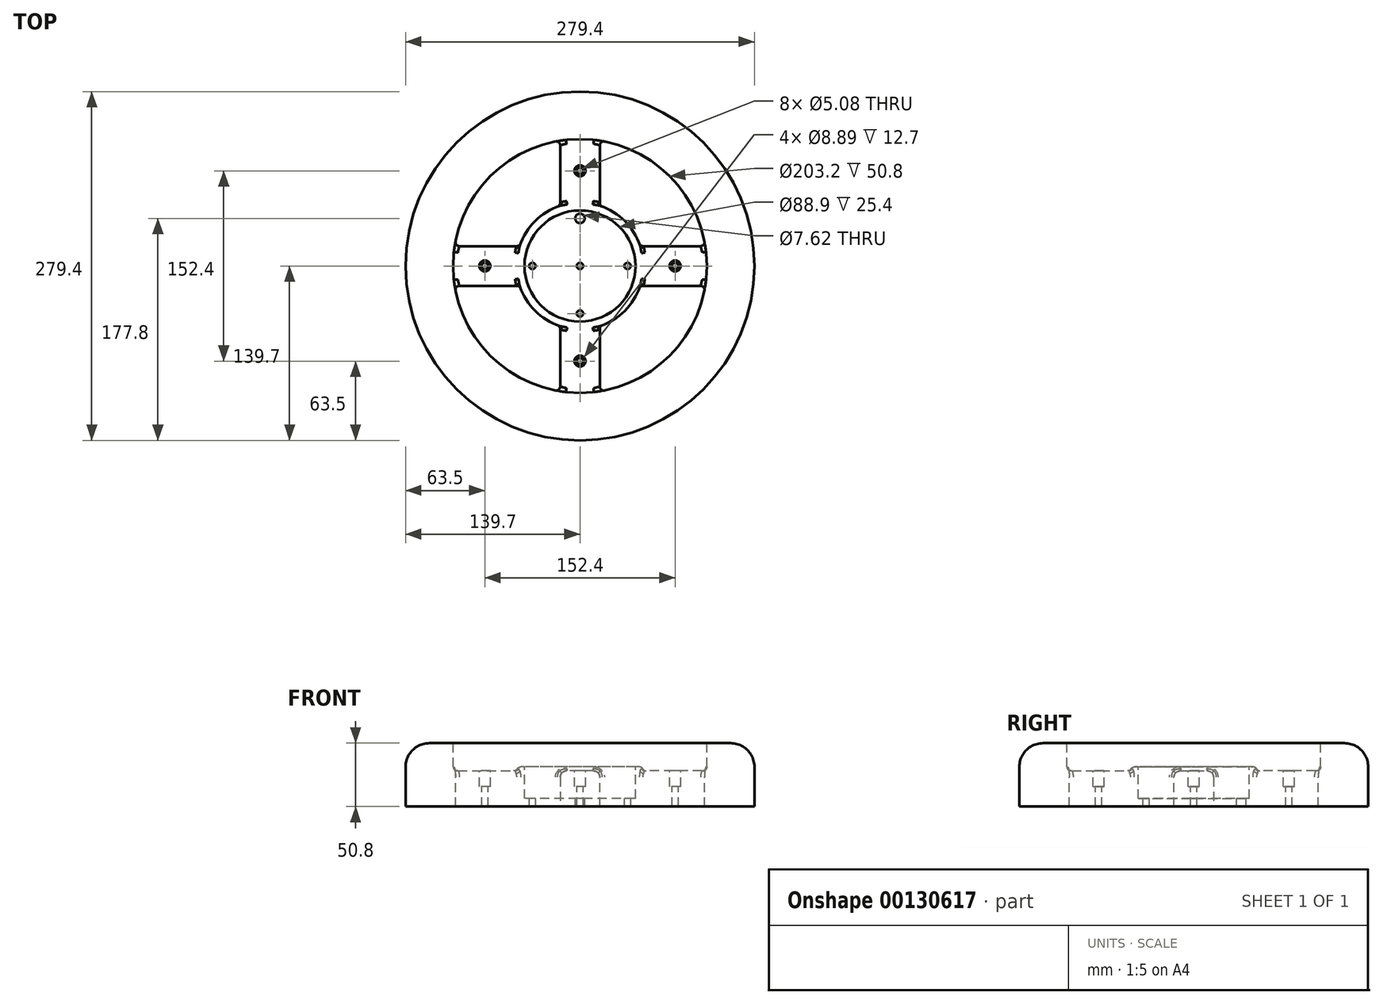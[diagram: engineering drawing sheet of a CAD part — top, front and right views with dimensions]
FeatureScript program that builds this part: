
annotation { "Feature Type Name" : "Feature", "Feature Type Description" : "" }
export const myFeature = defineFeature(function(context is Context, id is Id, definition is map)
    precondition{}
    {
        {
            var Q0;
            Q0=qCreatedBy(makeId("Top.planeOp"),FACE);
            var sketch = newSketch(context, id + "F0", { "sketchPlane" : qUnion([Q0])});
            skCircle(sketch, "E0", {"center": v(0, 0) * mm, "radius": 139.7 * mm});
            skSolve(sketch);
        }
        {
            var Q0;
            Q0 = qSketchRegion(id + "F0", true);
            extrude(context, id + "F1", {"entities" : qUnion([Q0]), "depth" : 50.8 * mm});
        }
        {
            var Q0;
            Q0=makeQuery(id+"F1.opExtrude","CAP_FACE",FACE,{"disambiguationData":[OSD([sQuery(id+"F0.wireOp",EDGE,"E0")])],"isStart":false});
            var sketch = newSketch(context, id + "F2", { "sketchPlane" : qUnion([Q0])});
            skCircle(sketch, "E1", {"center": v(0, 0) * mm, "radius": 101.6 * mm});
            skSolve(sketch);
        }
        {
            var Q0;
            Q0 = qSketchRegion(id + "F2", true);
            extrude(context, id + "F3", {"entities" : qUnion([Q0]), "operationType" : NewBodyOperationType.REMOVE, "oppositeDirection" : true, "depth" : 50.8 * mm});
        }
        {
            var Q0;
            Q0=makeQuery(id+"F1.opExtrude","CAP_EDGE",EDGE,{"disambiguationData":[OSD([sQuery(id+"F0.wireOp",EDGE,"E0")])],"isStart":false});
            var Q1;
            Q1=makeQuery(id+"F3.boolean.opBoolean","COPY",EDGE,{"derivedFrom":makeQuery(id+"F3.opExtrude","CAP_EDGE",EDGE,{"disambiguationData":[OSD([sQuery(id+"F2.wireOp",EDGE,"E1")])],"isStart":true})});
            fillet(context, id + "F4", {"entities" : qUnion([Q0, Q1]), "radius" : 19.05 * mm, "tangentPropagation" : true, "allowEdgeOverflow" : false});
        }
        {
            var Q0;
            Q0=qCreatedBy(makeId("Top.planeOp"),FACE);
            var sketch = newSketch(context, id + "F5", { "sketchPlane" : qUnion([Q0])});
            skCircle(sketch, "E2", {"center": v(0, 0) * mm, "radius": 50.8 * mm});
            skSolve(sketch);
        }
        {
            var Q0;
            Q0 = qSketchRegion(id + "F5", true);
            extrude(context, id + "F6", {"entities" : qUnion([Q0]), "depth" : 31.75 * mm});
        }
        {
            var Q0;
            Q0=makeQuery(id+"F6.opExtrude","CAP_FACE",FACE,{"disambiguationData":[OSD([sQuery(id+"F5.wireOp",EDGE,"E2")])],"isStart":false});
            var sketch = newSketch(context, id + "F7", { "sketchPlane" : qUnion([Q0])});
            skCircle(sketch, "E3", {"center": v(0, 0) * mm, "radius": 44.45 * mm});
            skSolve(sketch);
        }
        {
            var Q0;
            Q0 = qSketchRegion(id + "F7", true);
            extrude(context, id + "F8", {"entities" : qUnion([Q0]), "operationType" : NewBodyOperationType.REMOVE, "oppositeDirection" : true, "depth" : 25.4 * mm});
        }
        {
            var Q0;
            Q0=makeQuery(id+"F8.boolean.opBoolean","COPY",EDGE,{"derivedFrom":makeQuery(id+"F8.opExtrude","CAP_EDGE",EDGE,{"disambiguationData":[OSD([sQuery(id+"F7.wireOp",EDGE,"E3")])],"isStart":true})});
            var Q1;
            Q1=makeQuery(id+"F6.opExtrude","CAP_EDGE",EDGE,{"disambiguationData":[OSD([sQuery(id+"F5.wireOp",EDGE,"E2")])],"isStart":false});
            fillet(context, id + "F9", {"entities" : qUnion([Q0, Q1]), "radius" : 3.17 * mm, "tangentPropagation" : true, "allowEdgeOverflow" : false});
        }
        {
            var Q0;
            Q0=qCreatedBy(makeId("Top.planeOp"),FACE);
            var sketch = newSketch(context, id + "F10", { "sketchPlane" : qUnion([Q0])});
            skLineSegment(sketch, "E4.bottom", {"start": v(-15.87, 104.14) * mm, "end": v(15.88, 104.14) * mm});
            skLineSegment(sketch, "E4.top", {"start": v(-15.87, 47) * mm, "end": v(15.88, 47) * mm});
            skLineSegment(sketch, "E4.left", {"start": v(-15.87, 104.14) * mm, "end": v(-15.87, 47) * mm});
            skLineSegment(sketch, "E4.right", {"start": v(15.88, 104.14) * mm, "end": v(15.88, 47) * mm});
            skPoint(sketch, "E4.middle", {"position": v(0, 75.56) * mm});
            skLineSegment(sketch, "E5.bottom", {"start": v(15.88, -104.14) * mm, "end": v(-15.88, -104.14) * mm});
            skLineSegment(sketch, "E5.top", {"start": v(15.87, -47) * mm, "end": v(-15.88, -47) * mm});
            skLineSegment(sketch, "E5.left", {"start": v(15.88, -104.14) * mm, "end": v(15.87, -47) * mm});
            skLineSegment(sketch, "E5.right", {"start": v(-15.88, -104.14) * mm, "end": v(-15.88, -47) * mm});
            skPoint(sketch, "E5.middle", {"position": v(0, -75.56) * mm});
            skLineSegment(sketch, "E6.bottom", {"start": v(104.14, -15.87) * mm, "end": v(47, -15.87) * mm});
            skLineSegment(sketch, "E6.top", {"start": v(104.14, 15.88) * mm, "end": v(47, 15.88) * mm});
            skLineSegment(sketch, "E6.left", {"start": v(104.14, -15.87) * mm, "end": v(104.14, 15.88) * mm});
            skLineSegment(sketch, "E6.right", {"start": v(47, -15.87) * mm, "end": v(47, 15.88) * mm});
            skPoint(sketch, "E6.middle", {"position": v(75.56, 0) * mm});
            skLineSegment(sketch, "E7.bottom", {"start": v(-104.14, -15.88) * mm, "end": v(-47, -15.88) * mm});
            skLineSegment(sketch, "E7.top", {"start": v(-104.14, 15.88) * mm, "end": v(-47, 15.88) * mm});
            skLineSegment(sketch, "E7.left", {"start": v(-104.14, -15.88) * mm, "end": v(-104.14, 15.88) * mm});
            skLineSegment(sketch, "E7.right", {"start": v(-47, -15.88) * mm, "end": v(-47, 15.88) * mm});
            skPoint(sketch, "E7.middle", {"position": v(-75.57, 0) * mm});
            skSolve(sketch);
        }
        {
            var Q0;
            Q0 = qSketchRegion(id + "F10", true);
            extrude(context, id + "F11", {"entities" : qUnion([Q0]), "operationType" : NewBodyOperationType.ADD, "depth" : 28.57 * mm});
        }
        {
            var Q0;
            Q0=makeQuery(id+"F11.opExtrude","CAP_EDGE",EDGE,{"disambiguationData":[OSD([sQuery(id+"F10.wireOp",EDGE,"E5.right")])],"isStart":false});
            var Q1;
            Q1=makeQuery(id+"F11.opExtrude","CAP_EDGE",EDGE,{"disambiguationData":[OSD([sQuery(id+"F10.wireOp",EDGE,"E5.left")])],"isStart":false});
            var Q2;
            Q2=makeQuery(id+"F11.opExtrude","CAP_EDGE",EDGE,{"disambiguationData":[OSD([sQuery(id+"F10.wireOp",EDGE,"E6.bottom")])],"isStart":false});
            var Q3;
            Q3=makeQuery(id+"F11.opExtrude","CAP_EDGE",EDGE,{"disambiguationData":[OSD([sQuery(id+"F10.wireOp",EDGE,"E6.top")])],"isStart":false});
            var Q4;
            Q4=makeQuery(id+"F11.opExtrude","CAP_EDGE",EDGE,{"disambiguationData":[OSD([sQuery(id+"F10.wireOp",EDGE,"E4.right")])],"isStart":false});
            var Q5;
            Q5=makeQuery(id+"F11.opExtrude","CAP_EDGE",EDGE,{"disambiguationData":[OSD([sQuery(id+"F10.wireOp",EDGE,"E4.left")])],"isStart":false});
            var Q6;
            Q6=makeQuery(id+"F11.opExtrude","CAP_EDGE",EDGE,{"disambiguationData":[OSD([sQuery(id+"F10.wireOp",EDGE,"E7.top")])],"isStart":false});
            var Q7;
            Q7=makeQuery(id+"F11.opExtrude","CAP_EDGE",EDGE,{"disambiguationData":[OSD([sQuery(id+"F10.wireOp",EDGE,"E7.bottom")])],"isStart":false});
            fillet(context, id + "F12", {"entities" : qUnion([Q0, Q1, Q2, Q3, Q4, Q5, Q6, Q7]), "radius" : 5.08 * mm, "tangentPropagation" : true, "allowEdgeOverflow" : false});
        }
        {
            var Q0;
            Q0=makeQuery(id+"F11.boolean.opBoolean","INTERSECT",EDGE,{"derivedFrom":[makeQuery(id+"F6.opExtrude","SWEPT_FACE",FACE,{"disambiguationData":[OSD([sQuery(id+"F5.wireOp",EDGE,"E2")])]}),makeQuery(id+"F11.opExtrude","SWEPT_FACE",FACE,{"disambiguationData":[OSD([sQuery(id+"F10.wireOp",EDGE,"E5.right")])]})]});
            var Q1;
            {var subQ1=sQuery(id+"F10.wireOp",EDGE,"E5.right");var subQ8=sQuery(id+"F5.wireOp",EDGE,"E2");Q1=makeQuery(id+"F12.opFillet","BLEND_EDGE",EDGE,{"blendedFrom":[makeQuery(id+"F11.opExtrude","CAP_EDGE",EDGE,{"disambiguationData":[OSD([subQ1])],"isStart":false}),makeQuery(id+"F11.boolean.opBoolean","SPLIT",FACE,{"disambiguationData":[TD([makeQuery(id+"F11.opExtrude","SWEPT_FACE",FACE,{"disambiguationData":[OSD([subQ1])]})])],"derivedFrom":makeQuery(id+"F6.opExtrude","SWEPT_FACE",FACE,{"disambiguationData":[OSD([subQ8])]})})],"blendedInto":[makeQuery(id+"F11.boolean.opBoolean","SPLIT",FACE,{"disambiguationData":[TD([makeQuery(id+"F11.opExtrude","SWEPT_FACE",FACE,{"disambiguationData":[OSD([subQ1])]})])],"derivedFrom":makeQuery(id+"F6.opExtrude","SWEPT_FACE",FACE,{"disambiguationData":[OSD([subQ8])]})})]});}
            fillet(context, id + "F13", {"entities" : qUnion([Q0, Q1]), "radius" : 3.17 * mm, "tangentPropagation" : true, "allowEdgeOverflow" : false});
        }
        {
            var Q0;
            Q0=makeQuery(id+"F11.boolean.opBoolean","INTERSECT",EDGE,{"derivedFrom":[makeQuery(id+"F6.opExtrude","SWEPT_FACE",FACE,{"disambiguationData":[OSD([sQuery(id+"F5.wireOp",EDGE,"E2")])]}),makeQuery(id+"F11.opExtrude","SWEPT_FACE",FACE,{"disambiguationData":[OSD([sQuery(id+"F10.wireOp",EDGE,"E6.bottom")])]})]});
            var Q1;
            {var subQ0=sQuery(id+"F10.wireOp",EDGE,"E6.bottom");var subQ1=sQuery(id+"F10.wireOp",EDGE,"E5.left");var subQ8=sQuery(id+"F5.wireOp",EDGE,"E2");Q1=makeQuery(id+"F12.opFillet","BLEND_EDGE",EDGE,{"blendedFrom":[makeQuery(id+"F11.opExtrude","CAP_EDGE",EDGE,{"disambiguationData":[OSD([subQ0])],"isStart":false}),makeQuery(id+"F11.boolean.opBoolean","SPLIT",FACE,{"disambiguationData":[TD([makeQuery(id+"F11.opExtrude","SWEPT_FACE",FACE,{"disambiguationData":[OSD([subQ1])]})])],"derivedFrom":makeQuery(id+"F6.opExtrude","SWEPT_FACE",FACE,{"disambiguationData":[OSD([subQ8])]})})],"blendedInto":[makeQuery(id+"F11.boolean.opBoolean","SPLIT",FACE,{"disambiguationData":[TD([makeQuery(id+"F11.opExtrude","SWEPT_FACE",FACE,{"disambiguationData":[OSD([subQ1])]})])],"derivedFrom":makeQuery(id+"F6.opExtrude","SWEPT_FACE",FACE,{"disambiguationData":[OSD([subQ8])]})})]});}
            fillet(context, id + "F14", {"entities" : qUnion([Q0, Q1]), "radius" : 3.17 * mm, "tangentPropagation" : true, "allowEdgeOverflow" : false});
        }
        {
            var Q0;
            Q0=makeQuery(id+"F11.boolean.opBoolean","INTERSECT",EDGE,{"derivedFrom":[makeQuery(id+"F6.opExtrude","SWEPT_FACE",FACE,{"disambiguationData":[OSD([sQuery(id+"F5.wireOp",EDGE,"E2")])]}),makeQuery(id+"F11.opExtrude","SWEPT_FACE",FACE,{"disambiguationData":[OSD([sQuery(id+"F10.wireOp",EDGE,"E7.bottom")])]})]});
            var Q1;
            {var subQ0=sQuery(id+"F10.wireOp",EDGE,"E7.bottom");var subQ1=sQuery(id+"F10.wireOp",EDGE,"E5.right");var subQ8=sQuery(id+"F5.wireOp",EDGE,"E2");Q1=makeQuery(id+"F12.opFillet","BLEND_EDGE",EDGE,{"blendedFrom":[makeQuery(id+"F11.opExtrude","CAP_EDGE",EDGE,{"disambiguationData":[OSD([subQ0])],"isStart":false}),makeQuery(id+"F11.boolean.opBoolean","SPLIT",FACE,{"disambiguationData":[TD([makeQuery(id+"F11.opExtrude","SWEPT_FACE",FACE,{"disambiguationData":[OSD([subQ1])]})])],"derivedFrom":makeQuery(id+"F6.opExtrude","SWEPT_FACE",FACE,{"disambiguationData":[OSD([subQ8])]})})],"blendedInto":[makeQuery(id+"F11.boolean.opBoolean","SPLIT",FACE,{"disambiguationData":[TD([makeQuery(id+"F11.opExtrude","SWEPT_FACE",FACE,{"disambiguationData":[OSD([subQ1])]})])],"derivedFrom":makeQuery(id+"F6.opExtrude","SWEPT_FACE",FACE,{"disambiguationData":[OSD([subQ8])]})})]});}
            fillet(context, id + "F15", {"entities" : qUnion([Q0, Q1]), "radius" : 3.17 * mm, "tangentPropagation" : true, "allowEdgeOverflow" : false});
        }
        {
            var Q0;
            Q0=makeQuery(id+"F11.boolean.opBoolean","INTERSECT",EDGE,{"derivedFrom":[makeQuery(id+"F6.opExtrude","SWEPT_FACE",FACE,{"disambiguationData":[OSD([sQuery(id+"F5.wireOp",EDGE,"E2")])]}),makeQuery(id+"F11.opExtrude","SWEPT_FACE",FACE,{"disambiguationData":[OSD([sQuery(id+"F10.wireOp",EDGE,"E4.left")])]})]});
            var Q1;
            {var subQ0=sQuery(id+"F10.wireOp",EDGE,"E4.left");var subQ8=sQuery(id+"F5.wireOp",EDGE,"E2");Q1=makeQuery(id+"F12.opFillet","BLEND_EDGE",EDGE,{"blendedFrom":[makeQuery(id+"F11.opExtrude","CAP_EDGE",EDGE,{"disambiguationData":[OSD([subQ0])],"isStart":false}),makeQuery(id+"F11.boolean.opBoolean","SPLIT",FACE,{"disambiguationData":[TD([makeQuery(id+"F11.opExtrude","SWEPT_FACE",FACE,{"disambiguationData":[OSD([subQ0])]})])],"derivedFrom":makeQuery(id+"F6.opExtrude","SWEPT_FACE",FACE,{"disambiguationData":[OSD([subQ8])]})})],"blendedInto":[makeQuery(id+"F11.boolean.opBoolean","SPLIT",FACE,{"disambiguationData":[TD([makeQuery(id+"F11.opExtrude","SWEPT_FACE",FACE,{"disambiguationData":[OSD([subQ0])]})])],"derivedFrom":makeQuery(id+"F6.opExtrude","SWEPT_FACE",FACE,{"disambiguationData":[OSD([subQ8])]})})]});}
            fillet(context, id + "F16", {"entities" : qUnion([Q0, Q1]), "radius" : 3.17 * mm, "tangentPropagation" : true, "allowEdgeOverflow" : false});
        }
        {
            var Q0;
            Q0=makeQuery(id+"F11.opExtrude","CAP_FACE",FACE,{"disambiguationData":[OSD([sQuery(id+"F10.wireOp",EDGE,"E7.bottom"),sQuery(id+"F10.wireOp",EDGE,"E7.top"),sQuery(id+"F10.wireOp",EDGE,"E7.left"),sQuery(id+"F10.wireOp",EDGE,"E7.right")])],"isStart":false});
            var sketch = newSketch(context, id + "F17", { "sketchPlane" : qUnion([Q0])});
            skCircle(sketch, "E8", {"center": v(-76.2, 0) * mm, "radius": 4.45 * mm});
            skCircle(sketch, "E9", {"center": v(0, 76.2) * mm, "radius": 4.45 * mm});
            skCircle(sketch, "E10", {"center": v(76.2, 0) * mm, "radius": 4.45 * mm});
            skCircle(sketch, "E11", {"center": v(0, -76.2) * mm, "radius": 4.45 * mm});
            skSolve(sketch);
        }
        {
            var Q0;
            Q0 = qSketchRegion(id + "F17", true);
            extrude(context, id + "F18", {"entities" : qUnion([Q0]), "operationType" : NewBodyOperationType.REMOVE, "oppositeDirection" : true, "depth" : 12.7 * mm});
        }
        {
            var Q0;
            Q0=makeQuery(id+"F18.boolean.opBoolean","COPY",FACE,{"derivedFrom":makeQuery(id+"F18.opExtrude","CAP_FACE",FACE,{"disambiguationData":[OSD([sQuery(id+"F17.wireOp",EDGE,"E8")])],"isStart":false})});
            var sketch = newSketch(context, id + "F19", { "sketchPlane" : qUnion([Q0])});
            skCircle(sketch, "E12", {"center": v(-76.2, 0) * mm, "radius": 2.54 * mm});
            skCircle(sketch, "E13", {"center": v(0, 76.2) * mm, "radius": 2.54 * mm});
            skCircle(sketch, "E14", {"center": v(76.2, 0) * mm, "radius": 2.54 * mm});
            skCircle(sketch, "E15", {"center": v(0, -76.2) * mm, "radius": 2.54 * mm});
            skSolve(sketch);
        }
        {
            var Q0;
            Q0 = qSketchRegion(id + "F19", true);
            extrude(context, id + "F20", {"entities" : qUnion([Q0]), "operationType" : NewBodyOperationType.REMOVE, "endBound" : BoundingType.THROUGH_ALL, "oppositeDirection" : true, "depth" : 25.4 * mm});
        }
        {
            var Q0;
            Q0=makeQuery(id+"F8.boolean.opBoolean","COPY",FACE,{"derivedFrom":makeQuery(id+"F8.opExtrude","CAP_FACE",FACE,{"disambiguationData":[OSD([sQuery(id+"F7.wireOp",EDGE,"E3")])],"isStart":false})});
            var sketch = newSketch(context, id + "F21", { "sketchPlane" : qUnion([Q0])});
            skCircle(sketch, "E16", {"center": v(0, 38.1) * mm, "radius": 3.81 * mm});
            skSolve(sketch);
        }
        {
            var Q0;
            Q0 = qSketchRegion(id + "F21", true);
            extrude(context, id + "F22", {"entities" : qUnion([Q0]), "operationType" : NewBodyOperationType.REMOVE, "endBound" : BoundingType.THROUGH_ALL, "oppositeDirection" : true, "depth" : 25.4 * mm});
        }
        {
            var Q0;
            Q0=makeQuery(id+"F8.boolean.opBoolean","COPY",FACE,{"derivedFrom":makeQuery(id+"F8.opExtrude","CAP_FACE",FACE,{"disambiguationData":[OSD([sQuery(id+"F7.wireOp",EDGE,"E3")])],"isStart":false})});
            var sketch = newSketch(context, id + "F23", { "sketchPlane" : qUnion([Q0])});
            skCircle(sketch, "E17", {"center": v(0, 0) * mm, "radius": 2.54 * mm});
            skSolve(sketch);
        }
        {
            var Q0;
            Q0 = qSketchRegion(id + "F23", true);
            extrude(context, id + "F24", {"entities" : qUnion([Q0]), "operationType" : NewBodyOperationType.REMOVE, "endBound" : BoundingType.THROUGH_ALL, "oppositeDirection" : true, "depth" : 25.4 * mm});
        }
        {
            var Q0;
            Q0=makeQuery(id+"F8.boolean.opBoolean","COPY",FACE,{"derivedFrom":makeQuery(id+"F8.opExtrude","CAP_FACE",FACE,{"disambiguationData":[OSD([sQuery(id+"F7.wireOp",EDGE,"E3")])],"isStart":false})});
            var sketch = newSketch(context, id + "F25", { "sketchPlane" : qUnion([Q0])});
            skCircle(sketch, "E18", {"center": v(-38.1, 0) * mm, "radius": 2.54 * mm});
            skCircle(sketch, "E19", {"center": v(0, -38.1) * mm, "radius": 2.54 * mm});
            skCircle(sketch, "E20", {"center": v(38.1, 0) * mm, "radius": 2.54 * mm});
            skSolve(sketch);
        }
        {
            var Q0;
            Q0 = qSketchRegion(id + "F25", true);
            extrude(context, id + "F26", {"entities" : qUnion([Q0]), "operationType" : NewBodyOperationType.REMOVE, "endBound" : BoundingType.THROUGH_ALL, "oppositeDirection" : true, "depth" : 25.4 * mm});
        }
        {
            var Q0;
            Q0=makeQuery(id+"F11.boolean.opBoolean","INTERSECT",EDGE,{"derivedFrom":[makeQuery(id+"F3.boolean.opBoolean","COPY",FACE,{"derivedFrom":makeQuery(id+"F3.opExtrude","SWEPT_FACE",FACE,{"disambiguationData":[OSD([sQuery(id+"F2.wireOp",EDGE,"E1")])]})}),makeQuery(id+"F11.opExtrude","SWEPT_FACE",FACE,{"disambiguationData":[OSD([sQuery(id+"F10.wireOp",EDGE,"E6.bottom")])]})]});
            var Q1;
            Q1=makeQuery(id+"F12.opFillet","BLEND_EDGE",EDGE,{"blendedFrom":[makeQuery(id+"F11.opExtrude","CAP_EDGE",EDGE,{"disambiguationData":[OSD([sQuery(id+"F10.wireOp",EDGE,"E6.bottom")])],"isStart":false}),makeQuery(id+"F3.boolean.opBoolean","COPY",FACE,{"derivedFrom":makeQuery(id+"F3.opExtrude","SWEPT_FACE",FACE,{"disambiguationData":[OSD([sQuery(id+"F2.wireOp",EDGE,"E1")])]})})],"blendedInto":[makeQuery(id+"F3.boolean.opBoolean","COPY",FACE,{"derivedFrom":makeQuery(id+"F3.opExtrude","SWEPT_FACE",FACE,{"disambiguationData":[OSD([sQuery(id+"F2.wireOp",EDGE,"E1")])]})})]});
            fillet(context, id + "F27", {"entities" : qUnion([Q0, Q1]), "radius" : 3.17 * mm, "tangentPropagation" : true, "allowEdgeOverflow" : false});
        }
        {
            var Q0;
            Q0=makeQuery(id+"F11.boolean.opBoolean","INTERSECT",EDGE,{"derivedFrom":[makeQuery(id+"F3.boolean.opBoolean","COPY",FACE,{"derivedFrom":makeQuery(id+"F3.opExtrude","SWEPT_FACE",FACE,{"disambiguationData":[OSD([sQuery(id+"F2.wireOp",EDGE,"E1")])]})}),makeQuery(id+"F11.opExtrude","SWEPT_FACE",FACE,{"disambiguationData":[OSD([sQuery(id+"F10.wireOp",EDGE,"E4.right")])]})]});
            var Q1;
            Q1=makeQuery(id+"F12.opFillet","BLEND_EDGE",EDGE,{"blendedFrom":[makeQuery(id+"F11.opExtrude","CAP_EDGE",EDGE,{"disambiguationData":[OSD([sQuery(id+"F10.wireOp",EDGE,"E4.right")])],"isStart":false}),makeQuery(id+"F3.boolean.opBoolean","COPY",FACE,{"derivedFrom":makeQuery(id+"F3.opExtrude","SWEPT_FACE",FACE,{"disambiguationData":[OSD([sQuery(id+"F2.wireOp",EDGE,"E1")])]})})],"blendedInto":[makeQuery(id+"F3.boolean.opBoolean","COPY",FACE,{"derivedFrom":makeQuery(id+"F3.opExtrude","SWEPT_FACE",FACE,{"disambiguationData":[OSD([sQuery(id+"F2.wireOp",EDGE,"E1")])]})})]});
            fillet(context, id + "F28", {"entities" : qUnion([Q0, Q1]), "radius" : 3.17 * mm, "tangentPropagation" : true, "allowEdgeOverflow" : false});
        }
        {
            var Q0;
            Q0=makeQuery(id+"F12.opFillet","BLEND_EDGE",EDGE,{"blendedFrom":[makeQuery(id+"F11.opExtrude","CAP_EDGE",EDGE,{"disambiguationData":[OSD([sQuery(id+"F10.wireOp",EDGE,"E7.bottom")])],"isStart":false}),makeQuery(id+"F3.boolean.opBoolean","COPY",FACE,{"derivedFrom":makeQuery(id+"F3.opExtrude","SWEPT_FACE",FACE,{"disambiguationData":[OSD([sQuery(id+"F2.wireOp",EDGE,"E1")])]})})],"blendedInto":[makeQuery(id+"F3.boolean.opBoolean","COPY",FACE,{"derivedFrom":makeQuery(id+"F3.opExtrude","SWEPT_FACE",FACE,{"disambiguationData":[OSD([sQuery(id+"F2.wireOp",EDGE,"E1")])]})})]});
            var Q1;
            Q1=makeQuery(id+"F11.boolean.opBoolean","INTERSECT",EDGE,{"derivedFrom":[makeQuery(id+"F3.boolean.opBoolean","COPY",FACE,{"derivedFrom":makeQuery(id+"F3.opExtrude","SWEPT_FACE",FACE,{"disambiguationData":[OSD([sQuery(id+"F2.wireOp",EDGE,"E1")])]})}),makeQuery(id+"F11.opExtrude","SWEPT_FACE",FACE,{"disambiguationData":[OSD([sQuery(id+"F10.wireOp",EDGE,"E7.bottom")])]})]});
            fillet(context, id + "F29", {"entities" : qUnion([Q0, Q1]), "radius" : 3.17 * mm, "tangentPropagation" : true, "allowEdgeOverflow" : false});
        }
        {
            var Q0;
            Q0=makeQuery(id+"F12.opFillet","BLEND_EDGE",EDGE,{"blendedFrom":[makeQuery(id+"F11.opExtrude","CAP_EDGE",EDGE,{"disambiguationData":[OSD([sQuery(id+"F10.wireOp",EDGE,"E5.right")])],"isStart":false}),makeQuery(id+"F3.boolean.opBoolean","COPY",FACE,{"derivedFrom":makeQuery(id+"F3.opExtrude","SWEPT_FACE",FACE,{"disambiguationData":[OSD([sQuery(id+"F2.wireOp",EDGE,"E1")])]})})],"blendedInto":[makeQuery(id+"F3.boolean.opBoolean","COPY",FACE,{"derivedFrom":makeQuery(id+"F3.opExtrude","SWEPT_FACE",FACE,{"disambiguationData":[OSD([sQuery(id+"F2.wireOp",EDGE,"E1")])]})})]});
            var Q1;
            Q1=makeQuery(id+"F11.boolean.opBoolean","INTERSECT",EDGE,{"derivedFrom":[makeQuery(id+"F3.boolean.opBoolean","COPY",FACE,{"derivedFrom":makeQuery(id+"F3.opExtrude","SWEPT_FACE",FACE,{"disambiguationData":[OSD([sQuery(id+"F2.wireOp",EDGE,"E1")])]})}),makeQuery(id+"F11.opExtrude","SWEPT_FACE",FACE,{"disambiguationData":[OSD([sQuery(id+"F10.wireOp",EDGE,"E5.right")])]})]});
            fillet(context, id + "F30", {"entities" : qUnion([Q0, Q1]), "radius" : 3.17 * mm, "tangentPropagation" : true, "allowEdgeOverflow" : false});
        }
    });
